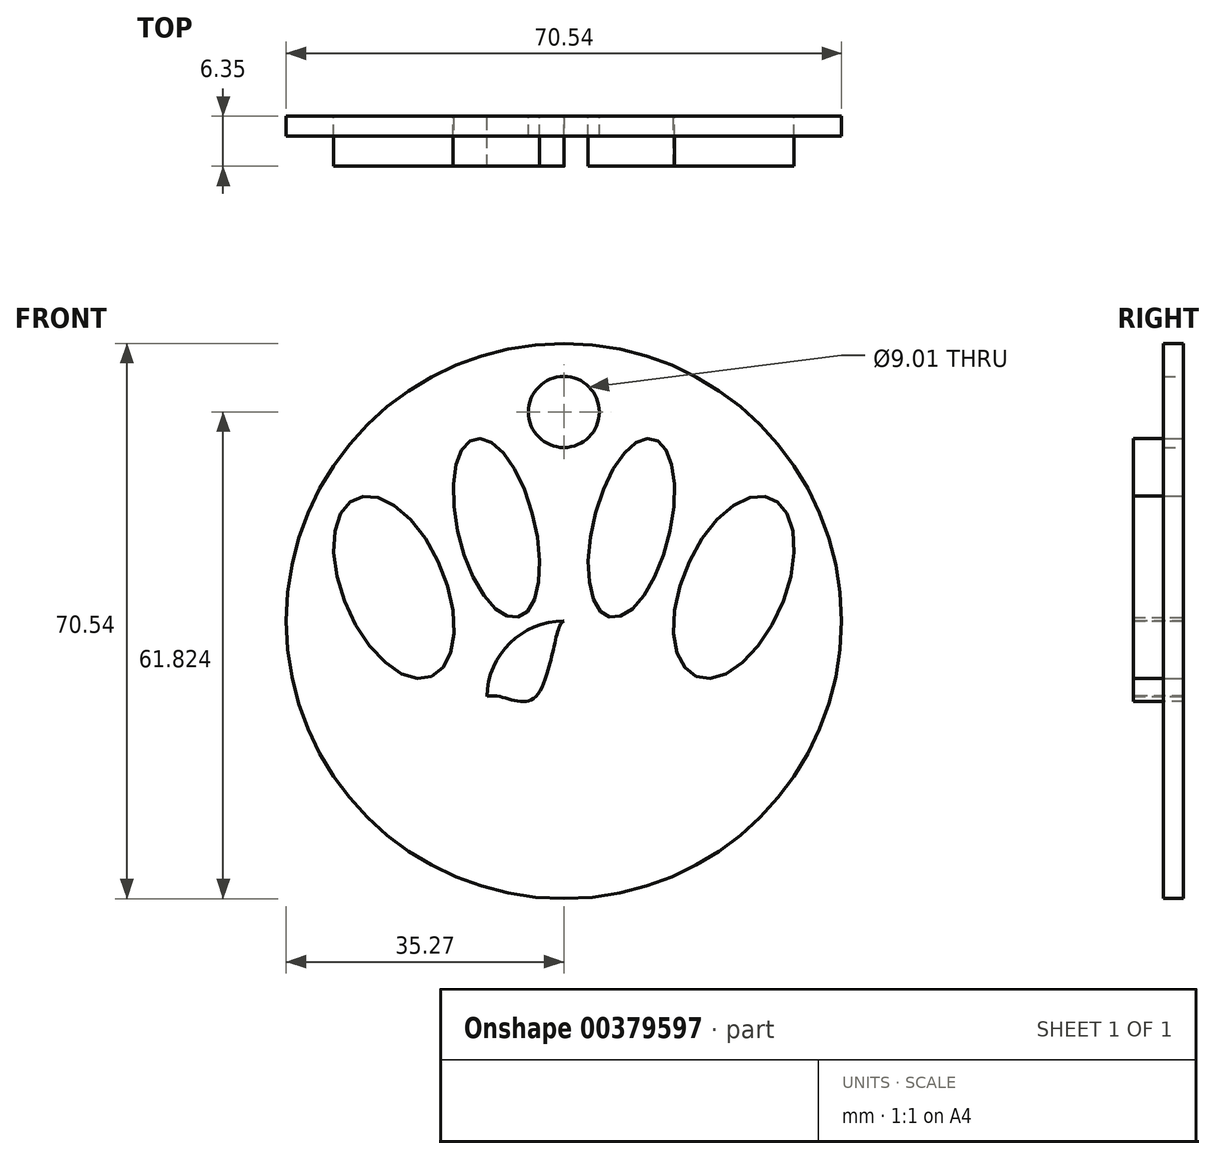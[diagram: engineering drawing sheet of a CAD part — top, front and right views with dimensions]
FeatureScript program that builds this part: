
annotation { "Feature Type Name" : "Feature", "Feature Type Description" : "" }
export const myFeature = defineFeature(function(context is Context, id is Id, definition is map)
    precondition{}
    {
        {
            var Q0;
            Q0=qCreatedBy(makeId("Front.planeOp"),FACE);
            var sketch = newSketch(context, id + "F0", { "sketchPlane" : qUnion([Q0])});
            skCircle(sketch, "E0", {"center": v(0, 0) * mm, "radius": 36.83 * mm});
            skArc(sketch, "E1", {"start": v(0, 0) * mm, "mid": v(-6.85, -2.8) * mm, "end": v(-9.77, -9.61) * mm});
            skFitSpline(sketch, "E2", {"points": [v(-9.77, -9.61) * mm, v(-13.7, -14.9) * mm, v(-20.9, -14.56) * mm, v(-21.59, -23.13) * mm, v(0, -27.59) * mm, v(0, 0) * mm, v(-3.77, -9.77) * mm, v(-9.77, -9.61) * mm]});
            skLineSegment(sketch, "E3", {"start": v(0, 36.83) * mm, "end": v(0, -36.83) * mm});
            skArc(sketch, "E4.MirrorCS", {"start": v(0, 0) * mm, "mid": v(6.85, -2.8) * mm, "end": v(9.77, -9.61) * mm});
            skFitSpline(sketch, "E5.MirrorCS", {"points": [v(9.77, -9.61) * mm, v(13.7, -14.9) * mm, v(20.9, -14.56) * mm, v(21.59, -23.13) * mm, v(0, -27.59) * mm, v(0, 0) * mm, v(3.77, -9.77) * mm, v(9.77, -9.61) * mm]});
            skFitSpline(sketch, "E6", {"points": [v(-5.13, -30.37) * mm, v(4.65, -30.28) * mm, v(3.43, -55.34) * mm, v(-5.13, -30.37) * mm]});
            skEllipse(sketch, "E7", {"center": v(-21.59, 4.28) * mm, "majorRadius": 12.28 * mm, "minorRadius": 6.48 * mm, "majorAxis": v(0.4, -0.92)});
            skEllipse(sketch, "E8", {"center": v(-8.57, 11.82) * mm, "majorRadius": 11.64 * mm, "minorRadius": 4.89 * mm, "majorAxis": v(0.24, -0.97)});
            skEllipse(sketch, "E9.MirrorC", {"center": v(8.57, 11.82) * mm, "majorRadius": 11.64 * mm, "minorRadius": 4.89 * mm, "majorAxis": v(-0.24, -0.97)});
            skEllipse(sketch, "E10.MirrorC", {"center": v(21.59, 4.28) * mm, "majorRadius": 12.28 * mm, "minorRadius": 6.48 * mm, "majorAxis": v(-0.4, -0.92)});
            skSolve(sketch);
        }
        {
            var Q0;
            Q0=makeQuery(id+"F0.imprint","IMPRINT",FACE,{"disambiguationData":[TD([[makeQuery(id+"F0.imprint","IMPRINT",EDGE,{"derivedFrom":sQuery(id+"F0.wireOp",EDGE,"E8")}),1.0]])]});
            var Q1;
            Q1=makeQuery(id+"F0.imprint","IMPRINT",FACE,{"disambiguationData":[TD([[makeQuery(id+"F0.imprint","IMPRINT",EDGE,{"derivedFrom":sQuery(id+"F0.wireOp",EDGE,"E7")}),1.0]])]});
            var Q2;
            Q2=makeQuery(id+"F0.imprint","IMPRINT",FACE,{"disambiguationData":[TD([[makeQuery(id+"F0.imprint","IMPRINT",EDGE,{"derivedFrom":sQuery(id+"F0.wireOp",EDGE,"E9.MirrorC")}),1.0]])]});
            var Q3;
            Q3=makeQuery(id+"F0.imprint","IMPRINT",FACE,{"disambiguationData":[TD([[makeQuery(id+"F0.imprint","IMPRINT",EDGE,{"derivedFrom":sQuery(id+"F0.wireOp",EDGE,"E10.MirrorC")}),1.0]])]});
            var Q4;
            {var subQ0=sQuery(id+"F0.wireOp",EDGE,"E4.MirrorCS");Q4=makeQuery(id+"F0.imprint","IMPRINT",FACE,{"disambiguationData":[TD([[makeQuery(id+"F0.imprint","IMPRINT",EDGE,{"derivedFrom":subQ0}),-1.0]])]});}
            var Q5;
            {var subQ0=sQuery(id+"F0.wireOp",EDGE,"E1");Q5=makeQuery(id+"F0.imprint","IMPRINT",FACE,{"disambiguationData":[TD([[makeQuery(id+"F0.imprint","IMPRINT",EDGE,{"derivedFrom":subQ0}),1.0]])]});}
            extrude(context, id + "F1", {"entities" : qUnion([Q0, Q1, Q2, Q3, Q4, Q5]), "depth" : 6.35 * mm});
        }
        {
            var Q0;
            Q0=qCreatedBy(makeId("Front.planeOp"),FACE);
            var sketch = newSketch(context, id + "F2", { "sketchPlane" : qUnion([Q0])});
            skCircle(sketch, "E11", {"center": v(0, 0) * mm, "radius": 40.98 * mm});
            skCircle(sketch, "E12", {"center": v(0, 0) * mm, "radius": 35.6 * mm});
            skSolve(sketch);
        }
        {
            var Q0;
            Q0=qSketchRegion(id+"F2",true);
            extrude(context, id + "F3", {"entities" : qUnion([Q0]), "depth" : 6.35 * mm});
        }
        {
            var Q0;
            Q0=makeQuery(id+"F3.opExtrude","SWEPT_BODY",BODY,{"disambiguationData":[OSD([sQuery(id+"F2.wireOp",EDGE,"E11"),sQuery(id+"F2.wireOp",EDGE,"E12")])]});
            deleteBodies(context, id + "F4", {"entities" : qUnion([Q0])});
        }
        {
            var Q0;
            Q0=qCreatedBy(makeId("Front.planeOp"),FACE);
            var sketch = newSketch(context, id + "F5", { "sketchPlane" : qUnion([Q0])});
            skCircle(sketch, "E13", {"center": v(0, 0) * mm, "radius": 35.27 * mm});
            skSolve(sketch);
        }
        {
            var Q0;
            Q0=makeQuery(id+"F5.imprint","IMPRINT",FACE,{"disambiguationData":[TD([[makeQuery(id+"F5.imprint","IMPRINT",EDGE,{"derivedFrom":sQuery(id+"F5.wireOp",EDGE,"E13")}),1.0]])]});
            extrude(context, id + "F6", {"entities" : qUnion([Q0]), "depth" : 2.54 * mm});
        }
        {
            var Q0;
            Q0=qCreatedBy(makeId("Front.planeOp"),FACE);
            var sketch = newSketch(context, id + "F7", { "sketchPlane" : qUnion([Q0])});
            skCircle(sketch, "E14", {"center": v(0, 26.55) * mm, "radius": 4.5 * mm});
            skSolve(sketch);
        }
        {
            var Q0;
            Q0=qSketchRegion(id+"F7",true);
            extrude(context, id + "F8", {"entities" : qUnion([Q0]), "operationType" : NewBodyOperationType.REMOVE, "depth" : 2.54 * mm});
        }
    });
